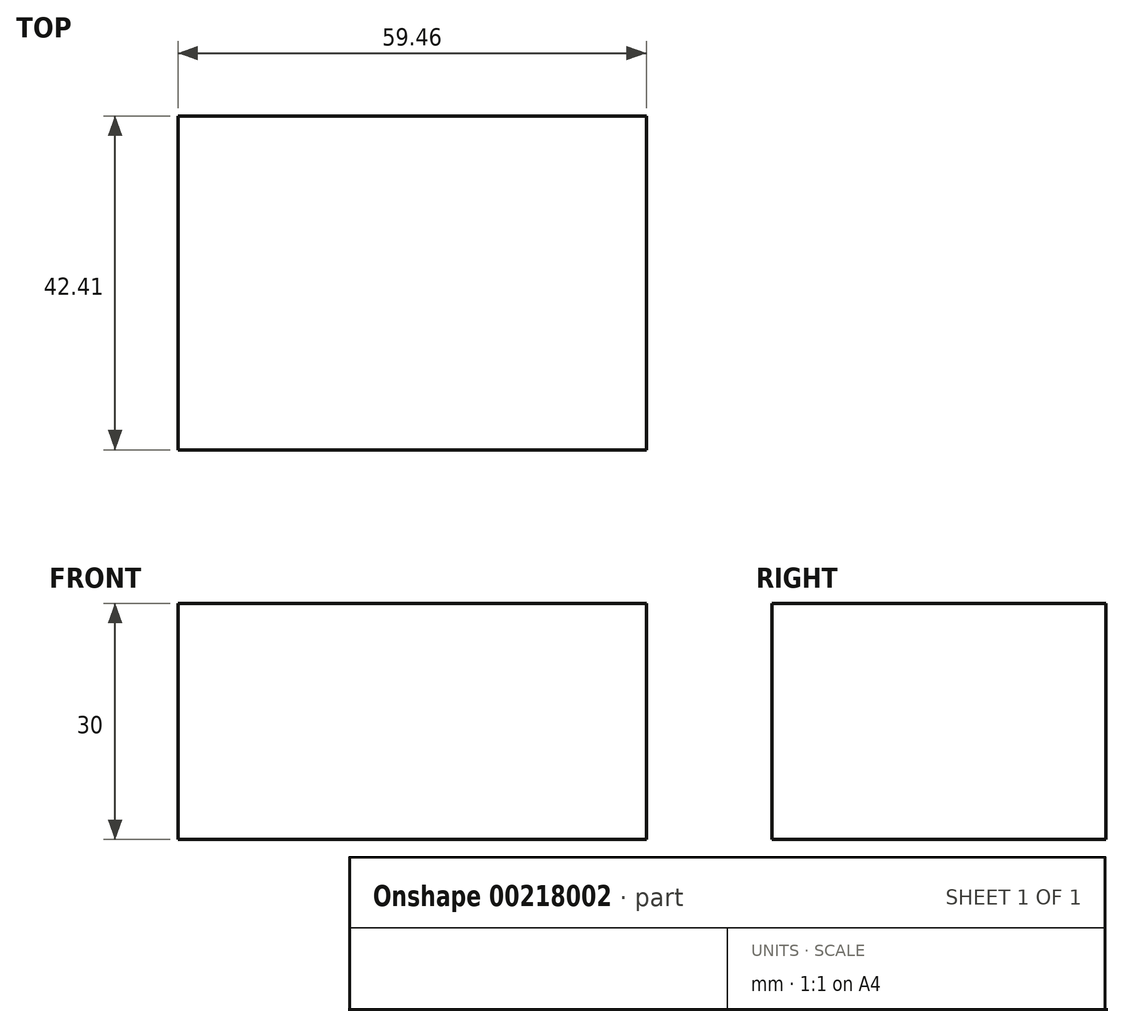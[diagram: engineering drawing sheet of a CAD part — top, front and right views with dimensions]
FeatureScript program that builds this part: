
annotation { "Feature Type Name" : "Feature", "Feature Type Description" : "" }
export const myFeature = defineFeature(function(context is Context, id is Id, definition is map)
    precondition{}
    {
        {
            var Q0;
            Q0=qCreatedBy(makeId("Top.planeOp"),FACE);
            var sketch = newSketch(context, id + "F0", { "sketchPlane" : qUnion([Q0])});
            skLineSegment(sketch, "E0.bottom", {"start": v(0, 0) * mm, "end": v(-59.46, 0) * mm});
            skLineSegment(sketch, "E0.top", {"start": v(0, 42.4) * mm, "end": v(-59.46, 42.4) * mm});
            skLineSegment(sketch, "E0.left", {"start": v(0, 0) * mm, "end": v(0, 42.4) * mm});
            skLineSegment(sketch, "E0.right", {"start": v(-59.46, 0) * mm, "end": v(-59.46, 42.4) * mm});
            skSolve(sketch);
        }
        {
            var Q0;
            Q0=makeQuery(id+"F0.imprint","IMPRINT",FACE,{"disambiguationData":[TD([[makeQuery(id+"F0.imprint","IMPRINT",EDGE,{"derivedFrom":sQuery(id+"F0.wireOp",EDGE,"E0.bottom")}),-1.0]])]});
            extrude(context, id + "F1", {"entities" : qUnion([Q0]), "depth" : 30 * mm});
        }
    });
